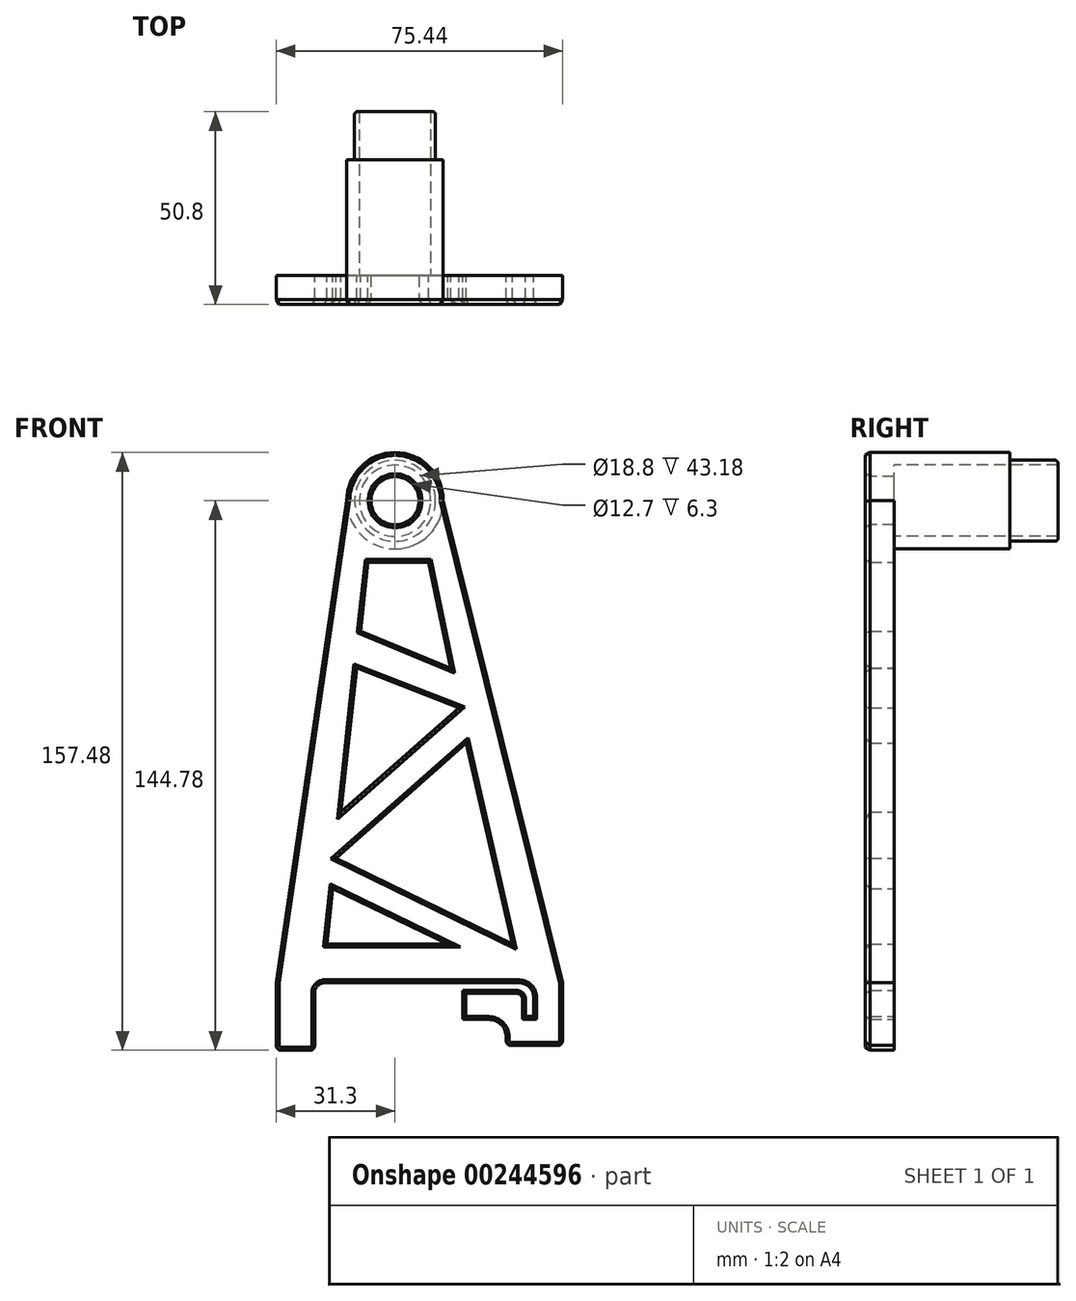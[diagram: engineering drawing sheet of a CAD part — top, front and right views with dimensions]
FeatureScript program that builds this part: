
annotation { "Feature Type Name" : "Feature", "Feature Type Description" : "" }
export const myFeature = defineFeature(function(context is Context, id is Id, definition is map)
    precondition{}
    {
        {
            var Q0;
            Q0=qCreatedBy(makeId("Front.planeOp"),FACE);
            var sketch = newSketch(context, id + "F0", { "sketchPlane" : qUnion([Q0])});
            skLineSegment(sketch, "E0", {"start": v(-18.6, 0) * mm, "end": v(32.7, 0) * mm});
            skLineSegment(sketch, "E1", {"start": v(36.52, -3.8) * mm, "end": v(36.52, -8.9) * mm});
            skLineSegment(sketch, "E2", {"start": v(36.52, -8.9) * mm, "end": v(34.36, -8.9) * mm});
            skLineSegment(sketch, "E3", {"start": v(30.55, -16.51) * mm, "end": v(42.87, -16.51) * mm});
            skLineSegment(sketch, "E4", {"start": v(44.14, -15.24) * mm, "end": v(44.14, 0) * mm});
            skLineSegment(sketch, "E5", {"start": v(44.14, 0) * mm, "end": v(12.7, 127) * mm});
            skLineSegment(sketch, "E6", {"start": v(-12.7, 127) * mm, "end": v(-31.3, 0) * mm});
            skLineSegment(sketch, "E7", {"start": v(-31.3, 0) * mm, "end": v(-31.3, -16.51) * mm});
            skLineSegment(sketch, "E8", {"start": v(-30.03, -17.78) * mm, "end": v(-22.41, -17.78) * mm});
            skLineSegment(sketch, "E9", {"start": v(-21.14, -16.51) * mm, "end": v(-21.14, -2.54) * mm});
            skArc(sketch, "E10", {"start": v(12.7, 127) * mm, "mid": v(0, 139.7) * mm, "end": v(-12.7, 127) * mm});
            skLineSegment(sketch, "E11", {"start": v(-17.5, 10.26) * mm, "end": v(13.86, 10.26) * mm});
            skLineSegment(sketch, "E12", {"start": v(8.87, 110.85) * mm, "end": v(-7.14, 110.85) * mm});
            skLineSegment(sketch, "E13", {"start": v(-7.14, 110.85) * mm, "end": v(-9.1, 92.68) * mm});
            skLineSegment(sketch, "E14", {"start": v(-17.99, 10.26) * mm, "end": v(-17.5, 10.26) * mm});
            skLineSegment(sketch, "E15", {"start": v(-15.55, 32.85) * mm, "end": v(18.8, 63.2) * mm});
            skLineSegment(sketch, "E16", {"start": v(-14.24, 45.02) * mm, "end": v(16.87, 72.47) * mm});
            skLineSegment(sketch, "E17", {"start": v(16.87, 72.47) * mm, "end": v(-10.15, 82.94) * mm});
            skLineSegment(sketch, "E18", {"start": v(-9.1, 92.68) * mm, "end": v(14.7, 82.88) * mm});
            skLineSegment(sketch, "E19", {"start": v(-15.55, 32.85) * mm, "end": v(30.9, 10.26) * mm});
            skLineSegment(sketch, "E20", {"start": v(-16.41, 24.87) * mm, "end": v(13.86, 10.26) * mm});
            skLineSegment(sketch, "E21.trimOffspring", {"start": v(-16.41, 24.87) * mm, "end": v(-17.99, 10.26) * mm});
            skLineSegment(sketch, "E22.trimOffspring", {"start": v(14.7, 82.88) * mm, "end": v(8.87, 110.85) * mm});
            skLineSegment(sketch, "E23.trimOffspring", {"start": v(-10.15, 82.94) * mm, "end": v(-14.24, 45.02) * mm});
            skLineSegment(sketch, "E24", {"start": v(18.8, 63.2) * mm, "end": v(30.9, 10.26) * mm});
            skLineSegment(sketch, "E25", {"start": v(29.28, -15.24) * mm, "end": v(29.28, -14.22) * mm});
            skLineSegment(sketch, "E26", {"start": v(29.28, -2.03) * mm, "end": v(32.07, -2.03) * mm});
            skLineSegment(sketch, "E27", {"start": v(34.36, -4.32) * mm, "end": v(34.36, -8.9) * mm});
            skPoint(sketch, "E28.visualSharp", {"position": v(36.52, 0) * mm});
            skArc(sketch, "E28.filletArc", {"start": v(36.52, -3.8) * mm, "mid": v(35.4, -1.12) * mm, "end": v(32.7, 0) * mm});
            skPoint(sketch, "E29.visualSharp", {"position": v(-21.14, 0) * mm});
            skArc(sketch, "E29.filletArc", {"start": v(-18.6, 0) * mm, "mid": v(-20.4, -0.74) * mm, "end": v(-21.14, -2.54) * mm});
            skLineSegment(sketch, "E30", {"start": v(29.28, -2.03) * mm, "end": v(17.85, -2.03) * mm});
            skLineSegment(sketch, "E31", {"start": v(17.85, -2.03) * mm, "end": v(17.85, -9.65) * mm});
            skLineSegment(sketch, "E32", {"start": v(17.85, -9.65) * mm, "end": v(24.7, -9.65) * mm});
            skPoint(sketch, "E33.visualSharp", {"position": v(34.36, -2.03) * mm});
            skArc(sketch, "E33.filletArc", {"start": v(34.36, -4.32) * mm, "mid": v(33.69, -2.7) * mm, "end": v(32.07, -2.03) * mm});
            skPoint(sketch, "E34.visualSharp", {"position": v(29.28, -9.65) * mm});
            skArc(sketch, "E34.filletArc", {"start": v(29.28, -14.22) * mm, "mid": v(27.94, -11) * mm, "end": v(24.7, -9.65) * mm});
            skPoint(sketch, "E35.visualSharp", {"position": v(29.28, -16.51) * mm});
            skArc(sketch, "E35.filletArc", {"start": v(29.28, -15.24) * mm, "mid": v(29.65, -16.14) * mm, "end": v(30.55, -16.51) * mm});
            skPoint(sketch, "E36.visualSharp", {"position": v(44.14, -16.5) * mm});
            skArc(sketch, "E36.filletArc", {"start": v(42.87, -16.5) * mm, "mid": v(43.76, -16.14) * mm, "end": v(44.14, -15.24) * mm});
            skPoint(sketch, "E37.visualSharp", {"position": v(-21.14, -17.78) * mm});
            skArc(sketch, "E37.filletArc", {"start": v(-22.41, -17.78) * mm, "mid": v(-21.51, -17.4) * mm, "end": v(-21.14, -16.51) * mm});
            skPoint(sketch, "E38.visualSharp", {"position": v(-31.3, -17.78) * mm});
            skArc(sketch, "E38.filletArc", {"start": v(-31.3, -16.51) * mm, "mid": v(-30.93, -17.4) * mm, "end": v(-30.03, -17.78) * mm});
            skSolve(sketch);
        }
        {
            var Q0;
            Q0=qSketchRegion(id+"F0",true);
            extrude(context, id + "F1", {"entities" : qUnion([Q0]), "depth" : 7.62 * mm});
        }
        {
            var Q0;
            Q0=makeQuery(id+"F1.opExtrude","CAP_FACE",FACE,{"disambiguationData":[OSD([sQuery(id+"F0.wireOp",EDGE,"E0"),sQuery(id+"F0.wireOp",EDGE,"E1"),sQuery(id+"F0.wireOp",EDGE,"E2"),sQuery(id+"F0.wireOp",EDGE,"E3"),sQuery(id+"F0.wireOp",EDGE,"E4"),sQuery(id+"F0.wireOp",EDGE,"E5"),sQuery(id+"F0.wireOp",EDGE,"E6"),sQuery(id+"F0.wireOp",EDGE,"E7"),sQuery(id+"F0.wireOp",EDGE,"E8"),sQuery(id+"F0.wireOp",EDGE,"E9"),sQuery(id+"F0.wireOp",EDGE,"85a4300b-4fb4-4320-8566-280c9bc53024"),sQuery(id+"F0.wireOp",EDGE,"pHLkkCRf-vtNH-Kyco-QB3F-mwyPBLed3uRI"),sQuery(id+"F0.wireOp",EDGE,"E10"),sQuery(id+"F0.wireOp",EDGE,"E11"),sQuery(id+"F0.wireOp",EDGE,"E12"),sQuery(id+"F0.wireOp",EDGE,"E13"),sQuery(id+"F0.wireOp",EDGE,"E14"),sQuery(id+"F0.wireOp",EDGE,"E15"),sQuery(id+"F0.wireOp",EDGE,"E16"),sQuery(id+"F0.wireOp",EDGE,"E17"),sQuery(id+"F0.wireOp",EDGE,"E18"),sQuery(id+"F0.wireOp",EDGE,"E19"),sQuery(id+"F0.wireOp",EDGE,"E20"),sQuery(id+"F0.wireOp",EDGE,"E21.trimOffspring"),sQuery(id+"F0.wireOp",EDGE,"E22.trimOffspring"),sQuery(id+"F0.wireOp",EDGE,"E23.trimOffspring"),sQuery(id+"F0.wireOp",EDGE,"E24")])],"isStart":false});
            var sketch = newSketch(context, id + "F2", { "sketchPlane" : qUnion([Q0])});
            skCircle(sketch, "E39", {"center": v(0, 127) * mm, "radius": 12.7 * mm});
            skCircle(sketch, "E40", {"center": v(0, 127) * mm, "radius": 9.4 * mm});
            skSolve(sketch);
        }
        {
            var Q0;
            Q0=qSketchRegion(id+"F2",true);
            extrude(context, id + "F3", {"entities" : qUnion([Q0]), "operationType" : NewBodyOperationType.ADD, "oppositeDirection" : true, "depth" : 38.1 * mm});
        }
        {
            var Q0;
            Q0=makeQuery(id+"F3.opExtrude","CAP_FACE",FACE,{"disambiguationData":[OSD([sQuery(id+"F2.wireOp",EDGE,"E39"),sQuery(id+"F2.wireOp",EDGE,"E40")])],"isStart":false});
            var sketch = newSketch(context, id + "F4", { "sketchPlane" : qUnion([Q0])});
            skCircle(sketch, "E41", {"center": v(0, 127) * mm, "radius": 10.67 * mm});
            skCircle(sketch, "E42", {"center": v(0, 127) * mm, "radius": 9.4 * mm});
            skSolve(sketch);
        }
        {
            var Q0;
            Q0=qSketchRegion(id+"F4",true);
            extrude(context, id + "F5", {"entities" : qUnion([Q0]), "operationType" : NewBodyOperationType.ADD, "depth" : 12.7 * mm});
        }
        {
            var Q0;
            Q0=makeQuery(id+"F3.boolean.opBoolean","SPLIT",FACE,{"disambiguationData":[TD([makeQuery(id+"F3.opExtrude","SWEPT_FACE",FACE,{"disambiguationData":[OSD([sQuery(id+"F2.wireOp",EDGE,"E40")])]})])],"derivedFrom":makeQuery(id+"F1.opExtrude","CAP_FACE",FACE,{"disambiguationData":[OSD([sQuery(id+"F0.wireOp",EDGE,"E0"),sQuery(id+"F0.wireOp",EDGE,"E1"),sQuery(id+"F0.wireOp",EDGE,"E2"),sQuery(id+"F0.wireOp",EDGE,"E3"),sQuery(id+"F0.wireOp",EDGE,"E4"),sQuery(id+"F0.wireOp",EDGE,"E5"),sQuery(id+"F0.wireOp",EDGE,"E6"),sQuery(id+"F0.wireOp",EDGE,"E7"),sQuery(id+"F0.wireOp",EDGE,"E8"),sQuery(id+"F0.wireOp",EDGE,"E9"),sQuery(id+"F0.wireOp",EDGE,"85a4300b-4fb4-4320-8566-280c9bc53024"),sQuery(id+"F0.wireOp",EDGE,"pHLkkCRf-vtNH-Kyco-QB3F-mwyPBLed3uRI"),sQuery(id+"F0.wireOp",EDGE,"E10"),sQuery(id+"F0.wireOp",EDGE,"E11"),sQuery(id+"F0.wireOp",EDGE,"E12"),sQuery(id+"F0.wireOp",EDGE,"E13"),sQuery(id+"F0.wireOp",EDGE,"E14"),sQuery(id+"F0.wireOp",EDGE,"E15"),sQuery(id+"F0.wireOp",EDGE,"E16"),sQuery(id+"F0.wireOp",EDGE,"E17"),sQuery(id+"F0.wireOp",EDGE,"E18"),sQuery(id+"F0.wireOp",EDGE,"E19"),sQuery(id+"F0.wireOp",EDGE,"E20"),sQuery(id+"F0.wireOp",EDGE,"E21.trimOffspring"),sQuery(id+"F0.wireOp",EDGE,"E22.trimOffspring"),sQuery(id+"F0.wireOp",EDGE,"E23.trimOffspring"),sQuery(id+"F0.wireOp",EDGE,"E24")])],"isStart":false})});
            var sketch = newSketch(context, id + "F6", { "sketchPlane" : qUnion([Q0])});
            skCircle(sketch, "E43", {"center": v(0, 127) * mm, "radius": 6.35 * mm});
            skSolve(sketch);
        }
        {
            var Q0;
            Q0=qSketchRegion(id+"F6",true);
            extrude(context, id + "F7", {"entities" : qUnion([Q0]), "operationType" : NewBodyOperationType.REMOVE, "oppositeDirection" : true, "depth" : 25.4 * mm});
        }
        {
            var Q0;
            Q0=makeQuery(id+"F1.opExtrude","CAP_FACE",FACE,{"disambiguationData":[OSD([sQuery(id+"F0.wireOp",EDGE,"E0"),sQuery(id+"F0.wireOp",EDGE,"E1"),sQuery(id+"F0.wireOp",EDGE,"E2"),sQuery(id+"F0.wireOp",EDGE,"E3"),sQuery(id+"F0.wireOp",EDGE,"E4"),sQuery(id+"F0.wireOp",EDGE,"E5"),sQuery(id+"F0.wireOp",EDGE,"E6"),sQuery(id+"F0.wireOp",EDGE,"E7"),sQuery(id+"F0.wireOp",EDGE,"E8"),sQuery(id+"F0.wireOp",EDGE,"E9"),sQuery(id+"F0.wireOp",EDGE,"E10"),sQuery(id+"F0.wireOp",EDGE,"E11"),sQuery(id+"F0.wireOp",EDGE,"E12"),sQuery(id+"F0.wireOp",EDGE,"E13"),sQuery(id+"F0.wireOp",EDGE,"E14"),sQuery(id+"F0.wireOp",EDGE,"E15"),sQuery(id+"F0.wireOp",EDGE,"E16"),sQuery(id+"F0.wireOp",EDGE,"E17"),sQuery(id+"F0.wireOp",EDGE,"E18"),sQuery(id+"F0.wireOp",EDGE,"E19"),sQuery(id+"F0.wireOp",EDGE,"E20"),sQuery(id+"F0.wireOp",EDGE,"E21.trimOffspring"),sQuery(id+"F0.wireOp",EDGE,"E22.trimOffspring"),sQuery(id+"F0.wireOp",EDGE,"E23.trimOffspring"),sQuery(id+"F0.wireOp",EDGE,"E24"),sQuery(id+"F0.wireOp",EDGE,"E25"),sQuery(id+"F0.wireOp",EDGE,"E26"),sQuery(id+"F0.wireOp",EDGE,"E27"),sQuery(id+"F0.wireOp",EDGE,"E28.filletArc"),sQuery(id+"F0.wireOp",EDGE,"E29.filletArc"),sQuery(id+"F0.wireOp",EDGE,"E30"),sQuery(id+"F0.wireOp",EDGE,"E31"),sQuery(id+"F0.wireOp",EDGE,"E32"),sQuery(id+"F0.wireOp",EDGE,"E33.filletArc"),sQuery(id+"F0.wireOp",EDGE,"E34.filletArc"),sQuery(id+"F0.wireOp",EDGE,"E35.filletArc"),sQuery(id+"F0.wireOp",EDGE,"E36.filletArc"),sQuery(id+"F0.wireOp",EDGE,"E37.filletArc"),sQuery(id+"F0.wireOp",EDGE,"E38.filletArc")])],"isStart":false});
            chamfer(context, id + "F8", {"entities" : qUnion([Q0]), "chamferType" : ChamferType.OFFSET_ANGLE, "width" : 0.76 * mm, "oppositeDirection" : false, "angle" : 60 * degree, "tangentPropagation" : true});
        }
        {
            var Q0;
            Q0=makeQuery(id+"F5.opExtrude","CAP_EDGE",EDGE,{"disambiguationData":[OSD([sQuery(id+"F4.wireOp",EDGE,"E41")])],"isStart":false});
            fillet(context, id + "F9", {"entities" : qUnion([Q0]), "radius" : 0.76 * mm, "tangentPropagation" : true, "allowEdgeOverflow" : false});
        }
    });
